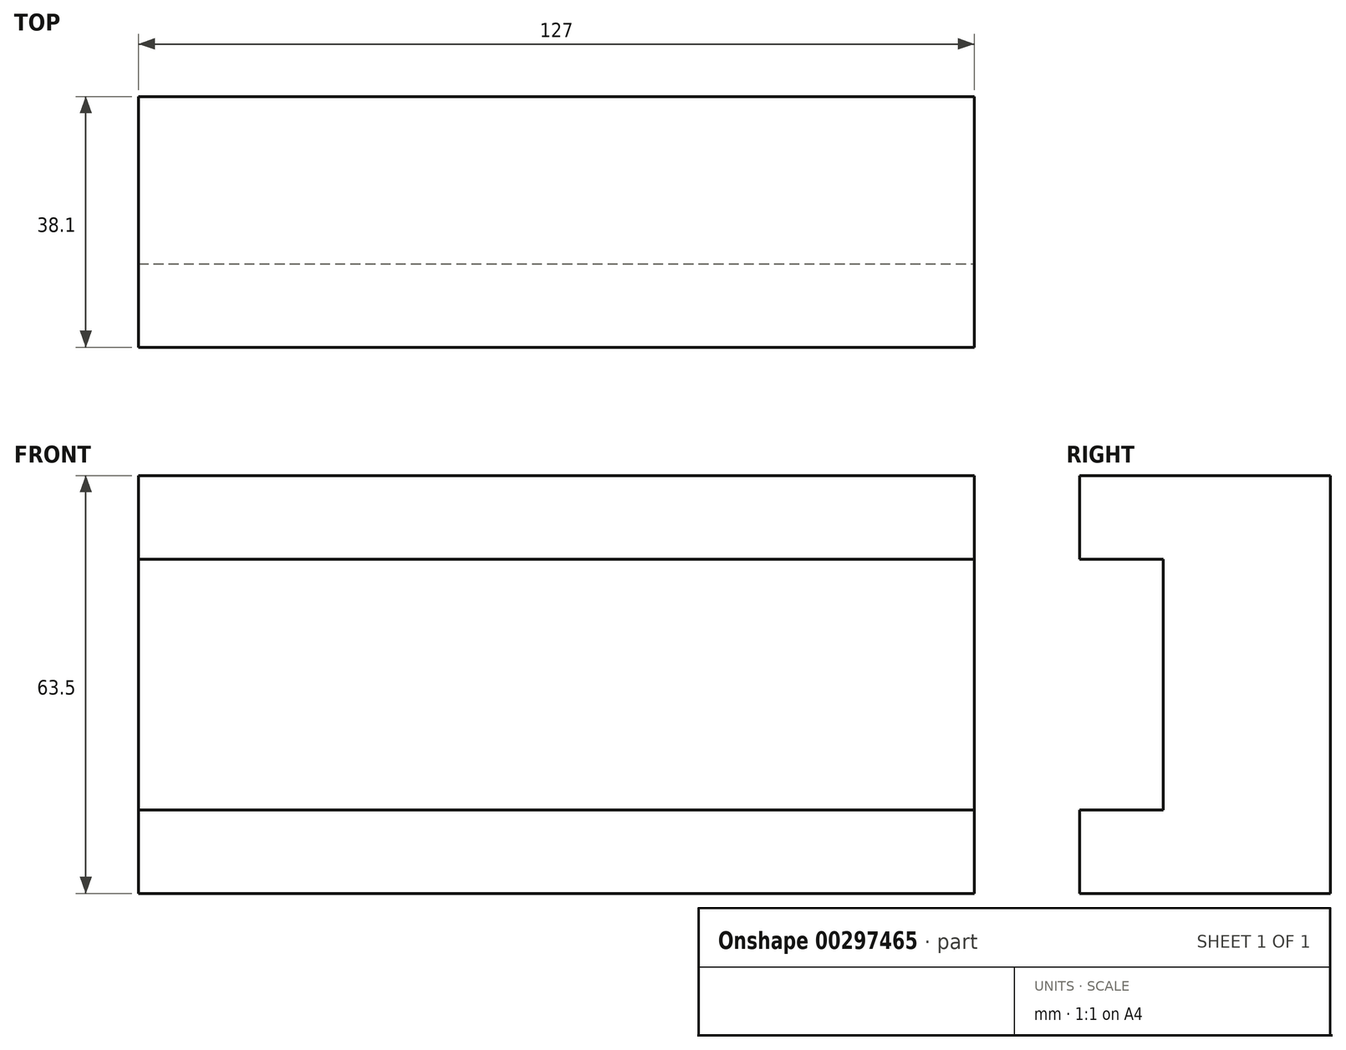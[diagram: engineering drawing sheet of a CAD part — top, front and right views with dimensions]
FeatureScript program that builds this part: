
annotation { "Feature Type Name" : "Feature", "Feature Type Description" : "" }
export const myFeature = defineFeature(function(context is Context, id is Id, definition is map)
    precondition{}
    {
        {
            var Q0;
            Q0=qCreatedBy(makeId("Front.planeOp"),FACE);
            var sketch = newSketch(context, id + "F0", { "sketchPlane" : qUnion([Q0])});
            skLineSegment(sketch, "E0.bottom", {"start": v(-63.5, 31.75) * mm, "end": v(63.5, 31.75) * mm});
            skLineSegment(sketch, "E0.top", {"start": v(-63.5, -31.75) * mm, "end": v(63.5, -31.75) * mm});
            skLineSegment(sketch, "E0.left", {"start": v(-63.5, 31.75) * mm, "end": v(-63.5, -31.75) * mm});
            skLineSegment(sketch, "E0.right", {"start": v(63.5, 31.75) * mm, "end": v(63.5, -31.75) * mm});
            skPoint(sketch, "E0.middle", {"position": v(0, 0) * mm});
            skSolve(sketch);
        }
        {
            var Q0;
            Q0 = qSketchRegion(id + "F0", true);
            extrude(context, id + "F1", {"entities" : qUnion([Q0]), "depth" : 25.4 * mm});
        }
        {
            var Q0;
            Q0=makeQuery(id+"F1.opExtrude","CAP_FACE",FACE,{"disambiguationData":[OSD([sQuery(id+"F0.wireOp",EDGE,"E0.bottom"),sQuery(id+"F0.wireOp",EDGE,"E0.top"),sQuery(id+"F0.wireOp",EDGE,"E0.left"),sQuery(id+"F0.wireOp",EDGE,"E0.right")])],"isStart":false});
            var sketch = newSketch(context, id + "F2", { "sketchPlane" : qUnion([Q0])});
            skLineSegment(sketch, "E1.bottom", {"start": v(-63.5, 19.05) * mm, "end": v(63.5, 19.05) * mm});
            skLineSegment(sketch, "E1.top", {"start": v(-63.5, 31.75) * mm, "end": v(63.5, 31.75) * mm});
            skLineSegment(sketch, "E1.left", {"start": v(-63.5, 19.05) * mm, "end": v(-63.5, 31.75) * mm});
            skLineSegment(sketch, "E1.right", {"start": v(63.5, 19.05) * mm, "end": v(63.5, 31.75) * mm});
            skSolve(sketch);
        }
        {
            var Q0;
            Q0 = qSketchRegion(id + "F2", true);
            extrude(context, id + "F3", {"entities" : qUnion([Q0]), "operationType" : NewBodyOperationType.ADD, "depth" : 12.7 * mm});
        }
        {
            var Q0;
            Q0=makeQuery(id+"F1.opExtrude","CAP_FACE",FACE,{"disambiguationData":[OSD([sQuery(id+"F0.wireOp",EDGE,"E0.bottom"),sQuery(id+"F0.wireOp",EDGE,"E0.top"),sQuery(id+"F0.wireOp",EDGE,"E0.left"),sQuery(id+"F0.wireOp",EDGE,"E0.right")])],"isStart":false});
            var sketch = newSketch(context, id + "F4", { "sketchPlane" : qUnion([Q0])});
            skLineSegment(sketch, "E2.bottom", {"start": v(-63.5, -19.05) * mm, "end": v(63.5, -19.05) * mm});
            skLineSegment(sketch, "E2.top", {"start": v(-63.5, -31.75) * mm, "end": v(63.5, -31.75) * mm});
            skLineSegment(sketch, "E2.left", {"start": v(-63.5, -19.05) * mm, "end": v(-63.5, -31.75) * mm});
            skLineSegment(sketch, "E2.right", {"start": v(63.5, -19.05) * mm, "end": v(63.5, -31.75) * mm});
            skSolve(sketch);
        }
        {
            var Q0;
            Q0 = qSketchRegion(id + "F4", true);
            extrude(context, id + "F5", {"entities" : qUnion([Q0]), "operationType" : NewBodyOperationType.ADD, "depth" : 12.7 * mm});
        }
    });
